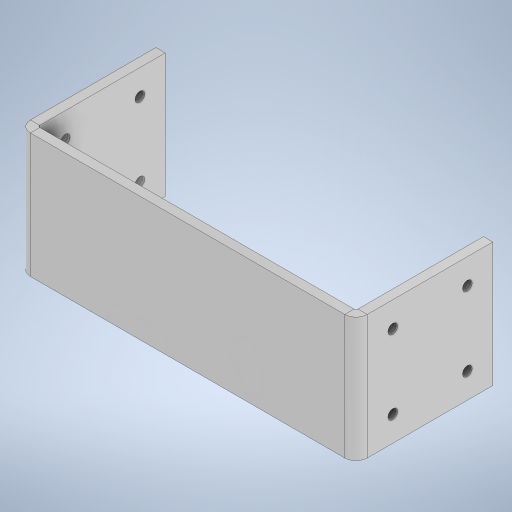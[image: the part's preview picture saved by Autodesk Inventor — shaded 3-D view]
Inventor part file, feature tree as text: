
AUTODESK INVENTOR PART (.ipt)
format: ipt  version: 2024.1 (Build 281209000, 209)  size: 262,144 bytes
history: native  units: in
note: dims shown in document units (in); Inventor stores cm internally (conversion verified against a paired STEP export)
features: sheet_metal_op x4, sketch x3, other x2, hole x1, projected_geometry x1
ambient origin geometry x8: Origin, YZ Plane, XZ Plane, XY Plane, X Axis, Y Axis, Z Axis, Center Point
bodies: Solid1 (feature_tree)
feature tree (11):
  sheet_metal_op  "Face1"
  sheet_metal_op  "Flange1"
  hole  "Hole1"  [1 undecoded]
  sketch  "Sketch1"  dims[d0=2.1331in d1=0.7874in]
  other  "Plate1"
  sketch  "Sketch2"  dims[d2=0.0591in]
  other  "Plate2"
  sheet_metal_op  "Bend1"
  sheet_metal_op  "Corner1"
  sketch  "Sketch3"  dims[d3=0.0591in d4=0.0295in d5=0.1181in d6=0.0122in d7=0.8661in d8=90.0deg d9=0.0122in d10=0.2362in d11=0.0591in d12=0.0122in d13=0.4724in d14=0.0617in d15=2.1331in d16=0.1575in d17=0.0787in d18=90.0deg d19=0.248in d20=0.8108in]
  projected_geometry  "Projected Loop1"
note: 1 required parameter value undecoded (feature->parameter linkage not recoverable at this tier; creation-order binding heuristic only, values carry confidence <= 0.55)
